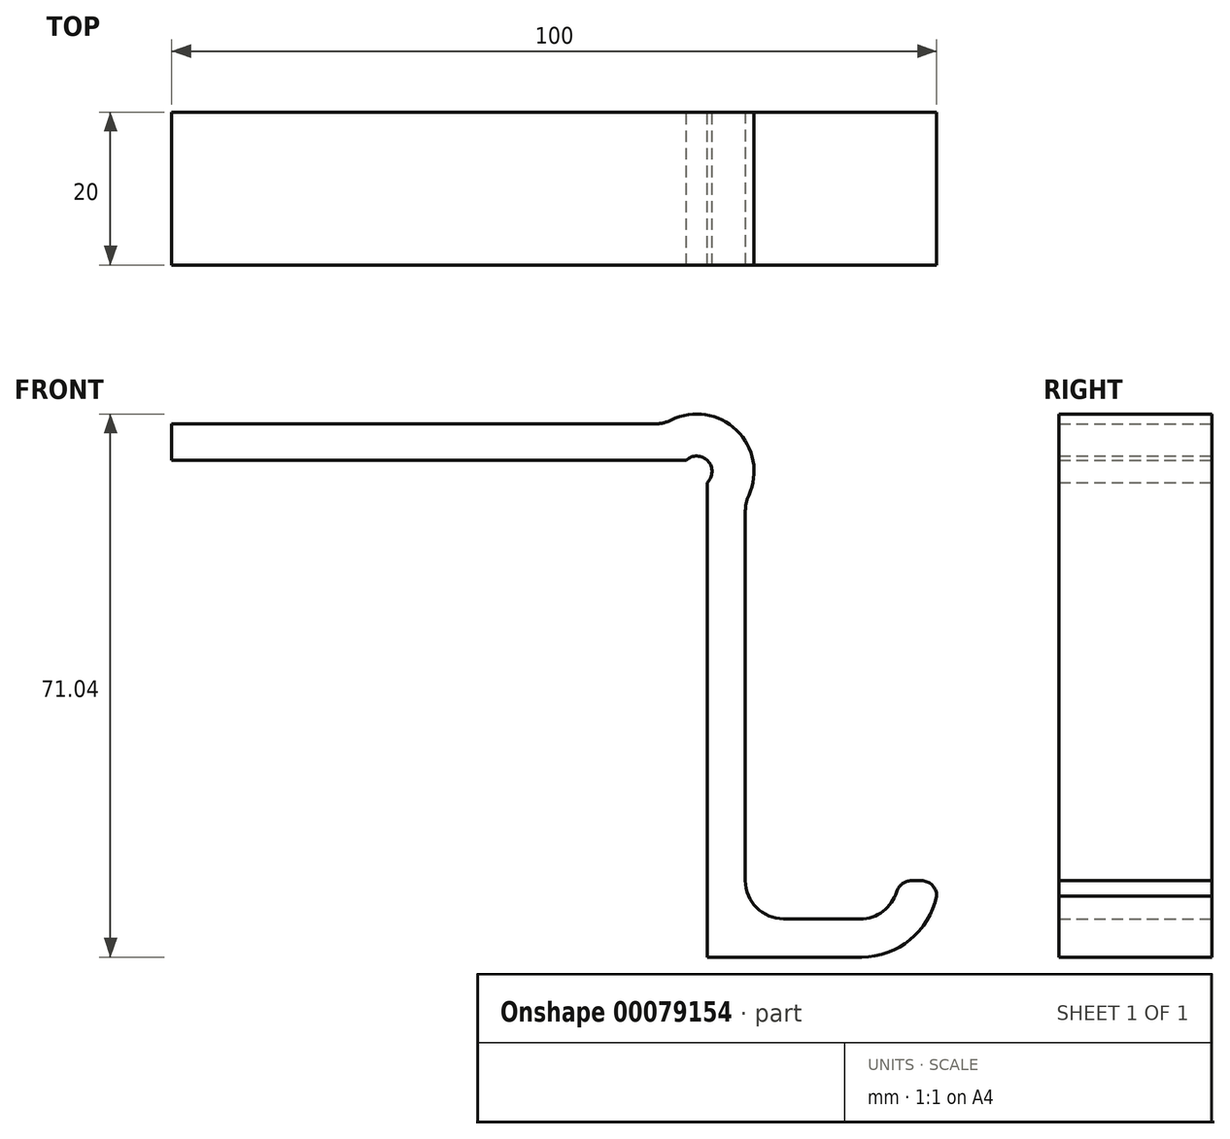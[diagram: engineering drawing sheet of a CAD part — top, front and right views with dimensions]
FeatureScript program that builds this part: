
annotation { "Feature Type Name" : "Feature", "Feature Type Description" : "" }
export const myFeature = defineFeature(function(context is Context, id is Id, definition is map)
    precondition{}
    {
        {
            var Q0;
            Q0=qCreatedBy(makeId("Front.planeOp"),FACE);
            var sketch = newSketch(context, id + "F0", { "sketchPlane" : qUnion([Q0]), "disableImprinting" : false});
            skLineSegment(sketch, "E0.left", {"start": v(0, 0) * mm, "end": v(0, 62.08) * mm});
            skLineSegment(sketch, "E0.right", {"start": v(5, 5) * mm, "end": v(5, 59.58) * mm});
            skLineSegment(sketch, "E1.top", {"start": v(5, 5) * mm, "end": v(25, 5) * mm});
            skLineSegment(sketch, "E2.top", {"start": v(30, 10) * mm, "end": v(25, 10) * mm});
            skLineSegment(sketch, "E2.right", {"start": v(25, 5) * mm, "end": v(25, 10) * mm});
            skLineSegment(sketch, "E3", {"start": v(30, 10) * mm, "end": v(30, 0) * mm});
            skLineSegment(sketch, "E4", {"start": v(30, 0) * mm, "end": v(0, 0) * mm});
            skLineSegment(sketch, "E5.top", {"start": v(-2.74, 65) * mm, "end": v(-70, 65) * mm});
            skLineSegment(sketch, "E5.right", {"start": v(-70, 69.74) * mm, "end": v(-70, 65) * mm});
            skLineSegment(sketch, "E6", {"start": v(-70, 69.74) * mm, "end": v(-5.59, 69.74) * mm});
            skArc(sketch, "E7", {"start": v(0, 62.08) * mm, "mid": v(0.09, 64.91) * mm, "end": v(-2.74, 65) * mm});
            skArc(sketch, "E8", {"start": v(5, 59.58) * mm, "mid": v(3.83, 68.95) * mm, "end": v(-5.59, 69.74) * mm});
            skPoint(sketch, "E9.orphan", {"position": v(0, 65) * mm});
            skSolve(sketch);
        }
        {
            var Q0;
            Q0=qSketchRegion(id+"F0",true);
            extrude(context, id + "F1", {"entities" : qUnion([Q0]), "depth" : 20 * mm});
        }
        {
            var Q0;
            Q0=makeQuery(id+"F1.opExtrude","SWEPT_EDGE",EDGE,{"disambiguationData":[OSD([sQuery(id+"F0.wireOp",EDGE,"E0.right"),sQuery(id+"F0.wireOp",EDGE,"E1.top")])]});
            var Q1;
            Q1=makeQuery(id+"F1.opExtrude","SWEPT_EDGE",EDGE,{"disambiguationData":[OSD([sQuery(id+"F0.wireOp",EDGE,"E1.top"),sQuery(id+"F0.wireOp",EDGE,"E2.right")])]});
            fillet(context, id + "F2", {"entities" : qUnion([Q0, Q1]), "radius" : 5 * mm, "tangentPropagation" : true, "allowEdgeOverflow" : false});
        }
        {
            var Q0;
            Q0=makeQuery(id+"F2.opFillet","BLEND_EDGE",EDGE,{"blendedFrom":[makeQuery(id+"F1.opExtrude","SWEPT_EDGE",EDGE,{"disambiguationData":[OSD([sQuery(id+"F0.wireOp",EDGE,"E1.top"),sQuery(id+"F0.wireOp",EDGE,"E2.right")])]}),makeQuery(id+"F1.opExtrude","SWEPT_FACE",FACE,{"disambiguationData":[OSD([sQuery(id+"F0.wireOp",EDGE,"E2.top")])]})],"blendedInto":[makeQuery(id+"F1.opExtrude","SWEPT_FACE",FACE,{"disambiguationData":[OSD([sQuery(id+"F0.wireOp",EDGE,"E2.top")])]})]});
            var Q1;
            Q1=makeQuery(id+"F1.opExtrude","SWEPT_EDGE",EDGE,{"disambiguationData":[OSD([sQuery(id+"F0.wireOp",EDGE,"E2.top"),sQuery(id+"F0.wireOp",EDGE,"E3")])]});
            fillet(context, id + "F3", {"entities" : qUnion([Q0, Q1]), "radius" : 2 * mm, "tangentPropagation" : true, "allowEdgeOverflow" : false});
        }
        {
            var Q0;
            Q0=makeQuery(id+"F1.opExtrude","SWEPT_EDGE",EDGE,{"disambiguationData":[OSD([sQuery(id+"F0.wireOp",EDGE,"E3"),sQuery(id+"F0.wireOp",EDGE,"E4")])]});
            fillet(context, id + "F4", {"entities" : qUnion([Q0]), "radius" : 10 * mm, "tangentPropagation" : true, "allowEdgeOverflow" : false});
        }
        {
            var Q0;
            Q0=makeQuery(id+"F1.opExtrude","SWEPT_EDGE",EDGE,{"disambiguationData":[OSD([sQuery(id+"F0.wireOp",EDGE,"E0.right"),sQuery(id+"F0.wireOp",EDGE,"E8")])]});
            var Q1;
            Q1=makeQuery(id+"F1.opExtrude","SWEPT_EDGE",EDGE,{"disambiguationData":[OSD([sQuery(id+"F0.wireOp",EDGE,"E6"),sQuery(id+"F0.wireOp",EDGE,"E8")])]});
            fillet(context, id + "F5", {"entities" : qUnion([Q0, Q1]), "radius" : 5 * mm, "tangentPropagation" : true, "allowEdgeOverflow" : false});
        }
    });
